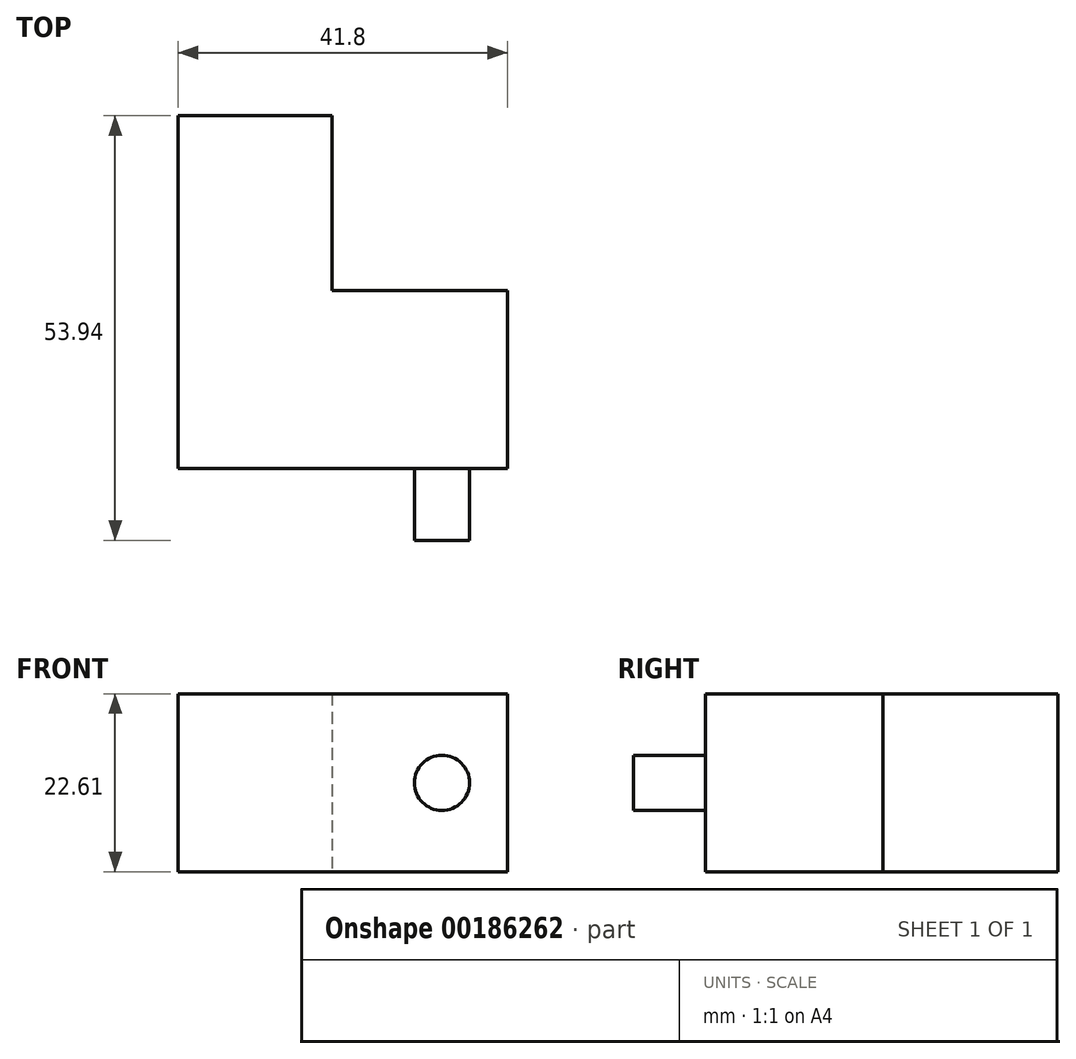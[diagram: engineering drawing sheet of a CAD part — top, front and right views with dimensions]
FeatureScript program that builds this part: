
annotation { "Feature Type Name" : "Feature", "Feature Type Description" : "" }
export const myFeature = defineFeature(function(context is Context, id is Id, definition is map)
    precondition{}
    {
        {
            var Q0;
            Q0=qCreatedBy(makeId("Top.planeOp"),FACE);
            var sketch = newSketch(context, id + "F0", { "sketchPlane" : qUnion([Q0])});
            skLineSegment(sketch, "E0.bottom", {"start": v(0, 0) * mm, "end": v(41.8, 0) * mm});
            skLineSegment(sketch, "E0.top", {"start": v(0, 44.8) * mm, "end": v(19.5, 44.8) * mm});
            skLineSegment(sketch, "E0.left", {"start": v(0, 0) * mm, "end": v(0, 44.8) * mm});
            skLineSegment(sketch, "E0.right", {"start": v(41.8, 0) * mm, "end": v(41.8, 22.6) * mm});
            skLineSegment(sketch, "E1", {"start": v(19.5, 44.8) * mm, "end": v(19.5, 22.6) * mm});
            skLineSegment(sketch, "E2", {"start": v(19.5, 22.6) * mm, "end": v(41.8, 22.6) * mm});
            skSolve(sketch);
        }
        {
            var Q0;
            Q0=makeQuery(id+"F0.imprint","IMPRINT",FACE,{"disambiguationData":[TD([[makeQuery(id+"F0.imprint","IMPRINT",EDGE,{"derivedFrom":sQuery(id+"F0.wireOp",EDGE,"E0.bottom")}),1.0]])]});
            extrude(context, id + "F1", {"entities" : qUnion([Q0]), "depth" : 22.6 * mm});
        }
        {
            var Q0;
            Q0=makeQuery(id+"F1.opExtrude","SWEPT_FACE",FACE,{"disambiguationData":[OSD([sQuery(id+"F0.wireOp",EDGE,"E0.bottom")])]});
            var sketch = newSketch(context, id + "F2", { "sketchPlane" : qUnion([Q0])});
            skCircle(sketch, "E3", {"center": v(33.5, 11.3) * mm, "radius": 3.5 * mm});
            skSolve(sketch);
        }
        {
            var Q0;
            Q0=makeQuery(id+"F2.imprint","IMPRINT",FACE,{"disambiguationData":[TD([[makeQuery(id+"F2.imprint","IMPRINT",EDGE,{"derivedFrom":sQuery(id+"F2.wireOp",EDGE,"E3")}),1.0]])]});
            extrude(context, id + "F3", {"entities" : qUnion([Q0]), "operationType" : NewBodyOperationType.ADD, "depth" : 9.14 * mm});
        }
    });
